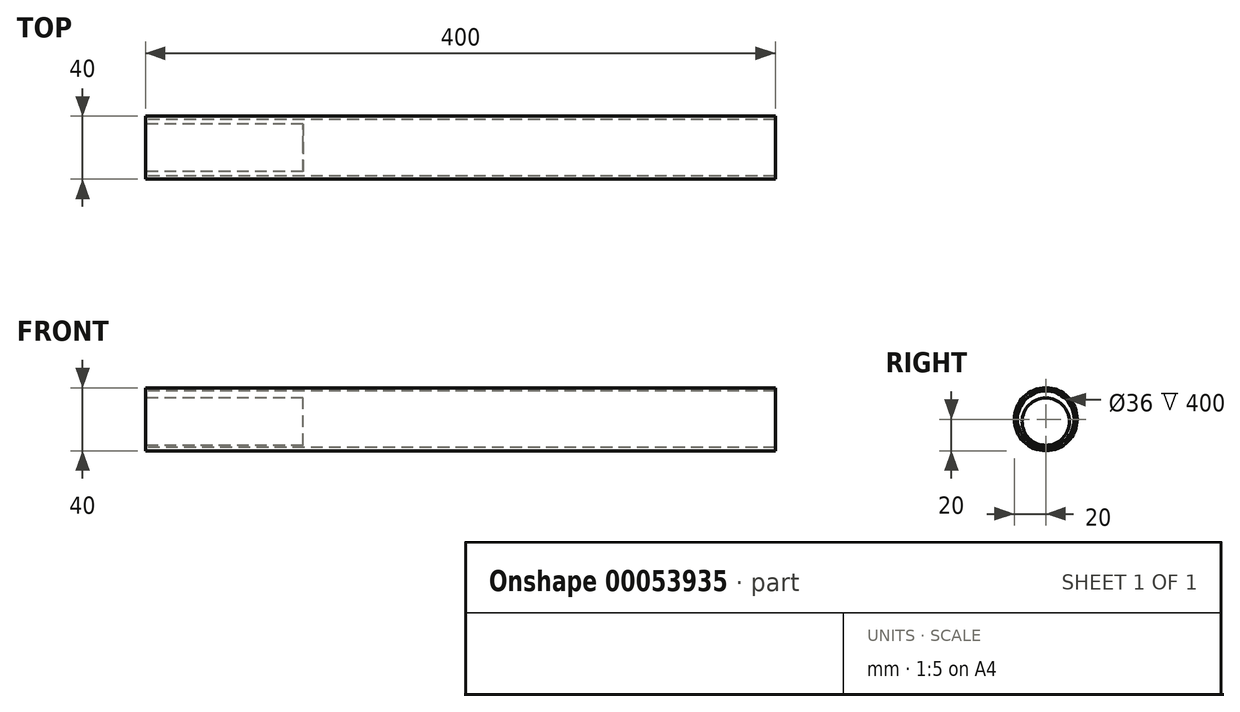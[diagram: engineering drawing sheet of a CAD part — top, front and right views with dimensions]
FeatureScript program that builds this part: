
annotation { "Feature Type Name" : "Feature", "Feature Type Description" : "" }
export const myFeature = defineFeature(function(context is Context, id is Id, definition is map)
    precondition{}
    {
        {
            var Q0;
            Q0=qCreatedBy(makeId("Right.planeOp"),FACE);
            var sketch = newSketch(context, id + "F0", { "sketchPlane" : qUnion([Q0])});
            skCircle(sketch, "E0", {"center": v(0, 0) * mm, "radius": 20 * mm});
            skCircle(sketch, "E1", {"center": v(0, 0) * mm, "radius": 18 * mm});
            skCircle(sketch, "E2", {"center": v(1.9, -3.3) * mm, "radius": 12.04 * mm});
            skSolve(sketch);
        }
        {
            var Q0;
            Q0=makeQuery(id+"F0.imprint","IMPRINT",FACE,{"disambiguationData":[TD([[makeQuery(id+"F0.imprint","IMPRINT",EDGE,{"derivedFrom":sQuery(id+"F0.wireOp",EDGE,"E0")}),1.0]])]});
            extrude(context, id + "F1", {"entities" : qUnion([Q0]), "depth" : 400 * mm});
        }
        {
            var Q0;
            Q0=qCreatedBy(makeId("Right.planeOp"),FACE);
            var sketch = newSketch(context, id + "F2", { "sketchPlane" : qUnion([Q0])});
            skCircle(sketch, "E3", {"center": v(0, -1.5) * mm, "radius": 15.05 * mm});
            skSolve(sketch);
        }
        {
            var Q0;
            Q0=makeQuery(id+"F2.imprint","IMPRINT",FACE,{"disambiguationData":[TD([[makeQuery(id+"F2.imprint","IMPRINT",EDGE,{"derivedFrom":sQuery(id+"F2.wireOp",EDGE,"E3")}),1.0]])]});
            extrude(context, id + "F3", {"entities" : qUnion([Q0]), "depth" : 100 * mm});
        }
    });
